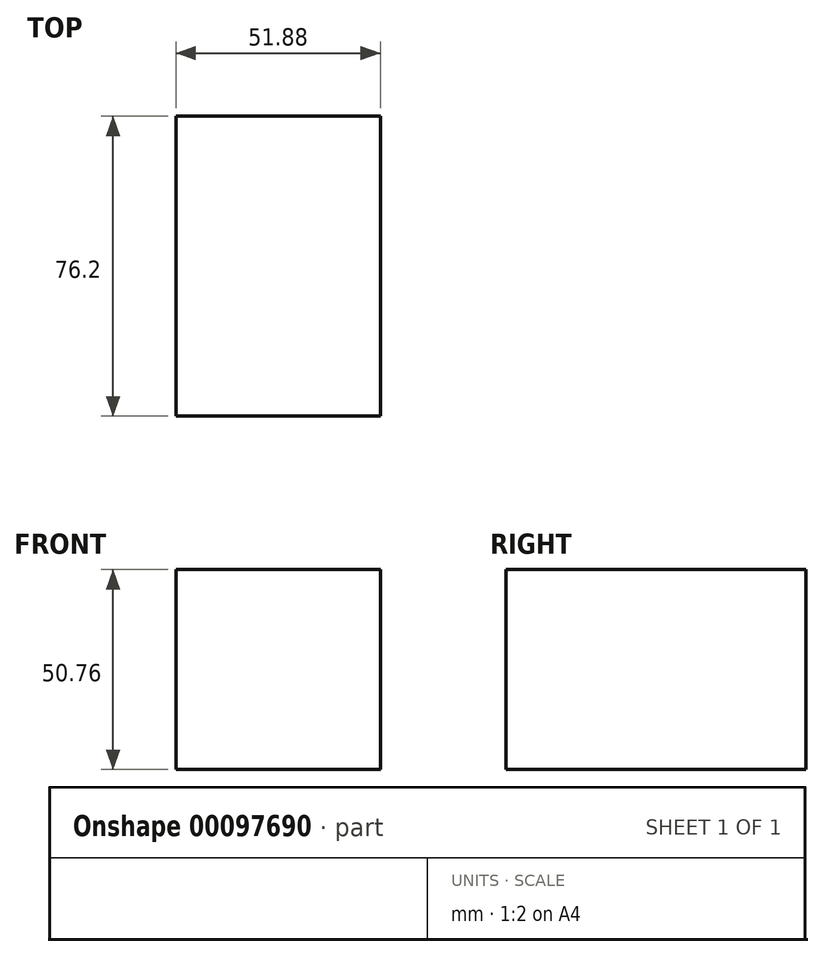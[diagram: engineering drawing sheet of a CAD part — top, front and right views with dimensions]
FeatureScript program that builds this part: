
annotation { "Feature Type Name" : "Feature", "Feature Type Description" : "" }
export const myFeature = defineFeature(function(context is Context, id is Id, definition is map)
    precondition{}
    {
        {
            var Q0;
            Q0=qCreatedBy(makeId("Front.planeOp"),FACE);
            var sketch = newSketch(context, id + "F0", { "sketchPlane" : qUnion([Q0])});
            skLineSegment(sketch, "E0.bottom", {"start": v(-17.89, 18.1) * mm, "end": v(33.99, 18.1) * mm});
            skLineSegment(sketch, "E0.top", {"start": v(-17.89, -32.67) * mm, "end": v(33.99, -32.67) * mm});
            skLineSegment(sketch, "E0.left", {"start": v(-17.89, 18.1) * mm, "end": v(-17.89, -32.67) * mm});
            skLineSegment(sketch, "E0.right", {"start": v(33.99, 18.1) * mm, "end": v(33.99, -32.67) * mm});
            skSolve(sketch);
        }
        {
            var Q0;
            Q0=makeQuery(id+"F0.imprint","IMPRINT",FACE,{"disambiguationData":[TD([[makeQuery(id+"F0.imprint","IMPRINT",EDGE,{"derivedFrom":sQuery(id+"F0.wireOp",EDGE,"E0.bottom")}),-1.0]])]});
            extrude(context, id + "F1", {"entities" : qUnion([Q0]), "depth" : 76.2 * mm});
        }
    });
